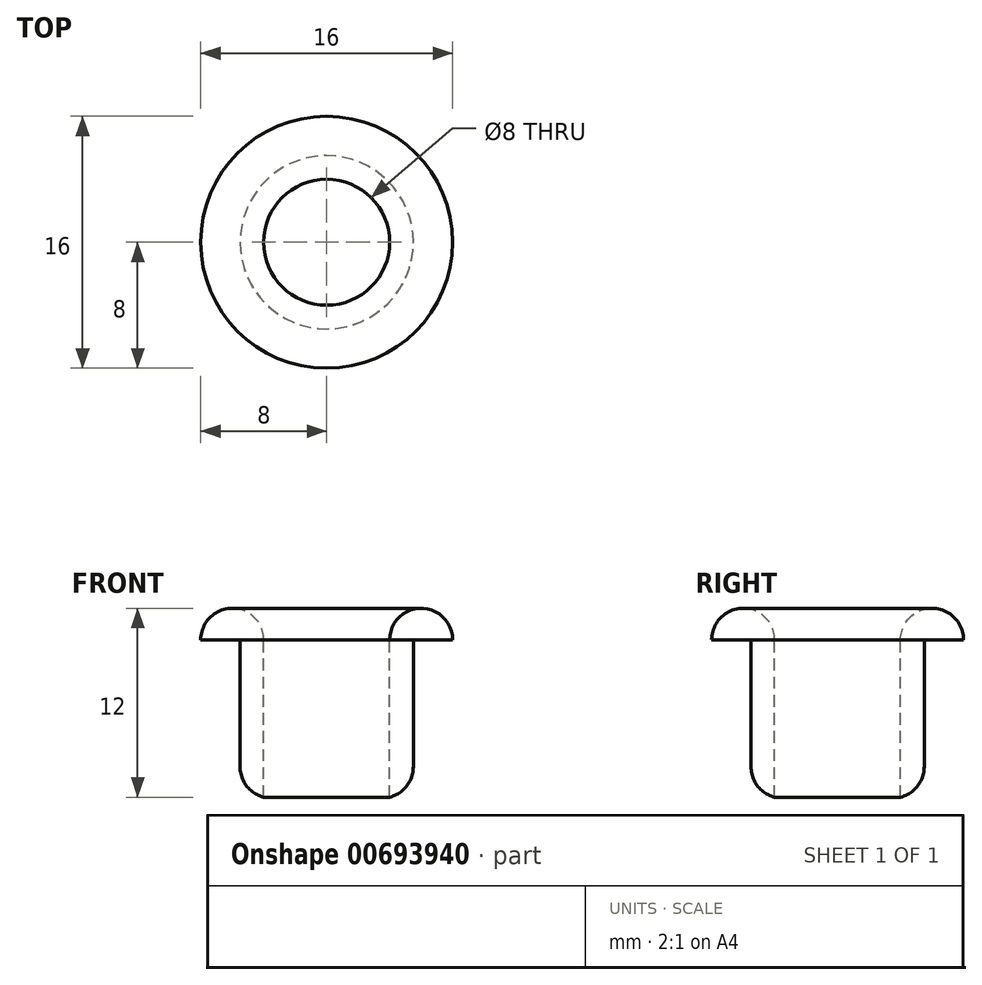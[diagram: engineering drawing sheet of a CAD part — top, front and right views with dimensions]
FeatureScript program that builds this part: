
annotation { "Feature Type Name" : "Feature", "Feature Type Description" : "" }
export const myFeature = defineFeature(function(context is Context, id is Id, definition is map)
    precondition{}
    {
        {
            var Q0;
            Q0=qCreatedBy(makeId("Top.planeOp"),FACE);
            var sketch = newSketch(context, id + "F0", { "sketchPlane" : qUnion([Q0])});
            skCircle(sketch, "E0", {"center": v(0, 0) * mm, "radius": 4 * mm});
            skCircle(sketch, "E1", {"center": v(0, 0) * mm, "radius": 5.5 * mm});
            skCircle(sketch, "E2", {"center": v(0, 0) * mm, "radius": 8 * mm});
            skSolve(sketch);
        }
        {
            var Q0;
            Q0=makeQuery(id+"F0.imprint","IMPRINT",FACE,{"disambiguationData":[TD([[makeQuery(id+"F0.imprint","IMPRINT",EDGE,{"derivedFrom":sQuery(id+"F0.wireOp",EDGE,"E0")}),-1.0]])]});
            extrude(context, id + "F1", {"entities" : qUnion([Q0]), "oppositeDirection" : true, "depth" : 10 * mm, "offsetDistance" : 25 * mm});
        }
        {
            var Q0;
            Q0=makeQuery(id+"F0.imprint","IMPRINT",FACE,{"disambiguationData":[TD([[makeQuery(id+"F0.imprint","IMPRINT",EDGE,{"derivedFrom":sQuery(id+"F0.wireOp",EDGE,"E1")}),-1.0]])]});
            var Q1;
            Q1=makeQuery(id+"F0.imprint","IMPRINT",FACE,{"disambiguationData":[TD([[makeQuery(id+"F0.imprint","IMPRINT",EDGE,{"derivedFrom":sQuery(id+"F0.wireOp",EDGE,"E0")}),-1.0]])]});
            extrude(context, id + "F2", {"entities" : qUnion([Q0, Q1]), "operationType" : NewBodyOperationType.ADD, "depth" : 2 * mm, "offsetDistance" : 25 * mm});
        }
        {
            var Q0;
            Q0=makeQuery(id+"F2.opExtrude","CAP_FACE",FACE,{"disambiguationData":[OSD([sQuery(id+"F0.wireOp",EDGE,"E0"),sQuery(id+"F0.wireOp",EDGE,"E2")])],"isStart":false});
            var Q1;
            Q1=makeQuery(id+"F1.opExtrude","CAP_EDGE",EDGE,{"disambiguationData":[OSD([sQuery(id+"F0.wireOp",EDGE,"E1")])],"isStart":false});
            fillet(context, id + "F3", {"entities" : qUnion([Q0, Q1]), "radius" : 2 * mm, "tangentPropagation" : true, "allowEdgeOverflow" : false});
        }
    });
